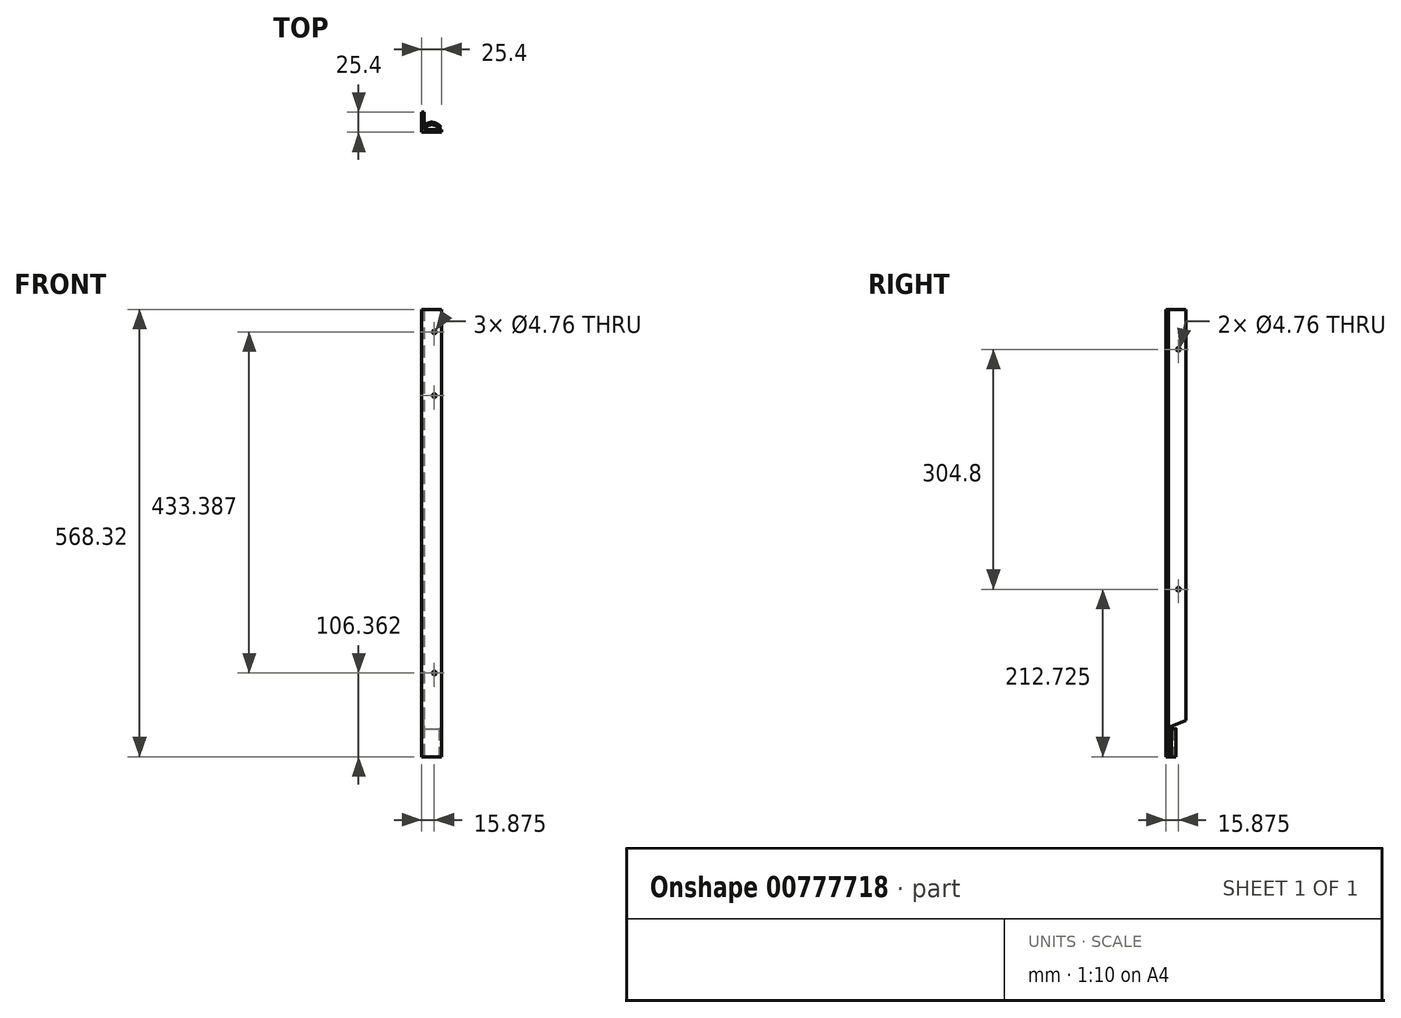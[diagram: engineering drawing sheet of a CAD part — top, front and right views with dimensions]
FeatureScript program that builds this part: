
annotation { "Feature Type Name" : "Feature", "Feature Type Description" : "" }
export const myFeature = defineFeature(function(context is Context, id is Id, definition is map)
    precondition{}
    {
        {
            var Q0;
            Q0=qCreatedBy(makeId("Top.planeOp"),FACE);
            var sketch = newSketch(context, id + "F0", { "sketchPlane" : qUnion([Q0])});
            skLineSegment(sketch, "E0.bottom", {"start": v(0, 0) * mm, "end": v(25.4, 0) * mm});
            skLineSegment(sketch, "E0.top", {"start": v(0, 25.4) * mm, "end": v(3.17, 25.4) * mm});
            skLineSegment(sketch, "E0.left", {"start": v(0, 0) * mm, "end": v(0, 25.4) * mm});
            skLineSegment(sketch, "E0.right", {"start": v(25.4, 0) * mm, "end": v(25.4, 3.18) * mm});
            skLineSegment(sketch, "E1.1", {"start": v(3.17, 3.18) * mm, "end": v(3.17, 25.4) * mm});
            skLineSegment(sketch, "E1.2", {"start": v(3.18, 3.18) * mm, "end": v(25.4, 3.18) * mm});
            skSolve(sketch);
        }
        {
            var Q0;
            Q0=qSketchRegion(id+"F0",true);
            extrude(context, id + "F1", {"entities" : qUnion([Q0]), "depth" : 568.32 * mm, "offsetDistance" : 25.4 * mm});
        }
        {
            var Q0;
            Q0=makeQuery(id+"F1.opExtrude","SWEPT_FACE",FACE,{"disambiguationData":[OSD([sQuery(id+"F0.wireOp",EDGE,"E0.left")])]});
            var sketch = newSketch(context, id + "F2", { "sketchPlane" : qUnion([Q0])});
            skCircle(sketch, "E2", {"center": v(-15.88, 517.53) * mm, "radius": 2.38 * mm});
            skCircle(sketch, "E3", {"center": v(-15.88, 212.73) * mm, "radius": 2.38 * mm});
            skSolve(sketch);
        }
        {
            var Q0;
            Q0=qSketchRegion(id+"F2",true);
            extrude(context, id + "F3", {"entities" : qUnion([Q0]), "operationType" : NewBodyOperationType.REMOVE, "oppositeDirection" : true, "depth" : 3.17 * mm, "offsetDistance" : 25.4 * mm});
        }
        {
            var Q0;
            Q0=makeQuery(id+"F1.opExtrude","SWEPT_FACE",FACE,{"disambiguationData":[OSD([sQuery(id+"F0.wireOp",EDGE,"E0.bottom")])]});
            var sketch = newSketch(context, id + "F4", { "sketchPlane" : qUnion([Q0])});
            skCircle(sketch, "E4", {"center": v(15.88, 458.79) * mm, "radius": 2.38 * mm});
            skCircle(sketch, "E5.0.1.0", {"center": v(15.88, 106.36) * mm, "radius": 2.38 * mm});
            skLineSegment(sketch, "E5.direction1", {"start": v(15.88, 458.79) * mm, "end": v(41.28, 458.79) * mm, "construction": true});
            skLineSegment(sketch, "E5.direction2", {"start": v(15.88, 458.79) * mm, "end": v(15.88, 106.36) * mm, "construction": true});
            skCircle(sketch, "E6", {"center": v(15.87, 539.75) * mm, "radius": 2.38 * mm});
            skSolve(sketch);
        }
        {
            var Q0;
            Q0=qSketchRegion(id+"F4",true);
            extrude(context, id + "F5", {"entities" : qUnion([Q0]), "operationType" : NewBodyOperationType.REMOVE, "oppositeDirection" : true, "depth" : 3.17 * mm, "offsetDistance" : 25.4 * mm});
        }
        {
            var Q0;
            Q0=makeQuery(id+"F1.opExtrude","SWEPT_FACE",FACE,{"disambiguationData":[OSD([sQuery(id+"F0.wireOp",EDGE,"E0.left")])]});
            var sketch = newSketch(context, id + "F6", { "sketchPlane" : qUnion([Q0])});
            skLineSegment(sketch, "E7", {"start": v(-4.76, 0) * mm, "end": v(-4.76, 38.1) * mm});
            skLineSegment(sketch, "E8", {"start": v(-4.76, 38.1) * mm, "end": v(-25.4, 46.44) * mm});
            skSolve(sketch);
        }
        {
            var Q0;
            Q0=qSketchRegion(id+"F6",true);
            var Q1;
            {var subQ0=sQuery(id+"F6.wireOp",EDGE,"E7");Q1=makeQuery(id+"F6.imprint","IMPRINT",FACE,{"disambiguationData":[TD([[makeQuery(id+"F6.imprint","IMPRINT",EDGE,{"derivedFrom":subQ0}),1.0]])]});}
            extrude(context, id + "F7", {"entities" : qUnion([Q0, Q1]), "operationType" : NewBodyOperationType.REMOVE, "oppositeDirection" : true, "depth" : 3.17 * mm, "offsetDistance" : 25.4 * mm});
        }
        {
            var Q0;
            Q0=makeQuery(id+"F1.opExtrude","CAP_FACE",FACE,{"disambiguationData":[OSD([sQuery(id+"F0.wireOp",EDGE,"E0.bottom"),sQuery(id+"F0.wireOp",EDGE,"E0.top"),sQuery(id+"F0.wireOp",EDGE,"E0.left"),sQuery(id+"F0.wireOp",EDGE,"E0.right"),sQuery(id+"F0.wireOp",EDGE,"E1.1"),sQuery(id+"F0.wireOp",EDGE,"E1.2")])],"isStart":true});
            var sketch = newSketch(context, id + "F8", { "sketchPlane" : qUnion([Q0])});
            skArc(sketch, "E9", {"start": v(12.36, -9.5) * mm, "mid": v(12.7, -9.53) * mm, "end": v(13.04, -9.5) * mm});
            skArc(sketch, "E10.0", {"start": v(12.01, -12.66) * mm, "mid": v(12.7, -12.7) * mm, "end": v(13.39, -12.66) * mm});
            skArc(sketch, "E11", {"start": v(0, -4.76) * mm, "mid": v(0.2, -5.89) * mm, "end": v(0.8, -6.87) * mm});
            skArc(sketch, "E12", {"start": v(0.8, -6.87) * mm, "mid": v(5.87, -10.81) * mm, "end": v(12.01, -12.66) * mm});
            skArc(sketch, "E13.0", {"start": v(3.17, -4.76) * mm, "mid": v(7.32, -7.99) * mm, "end": v(12.36, -9.5) * mm});
            skLineSegment(sketch, "E14", {"start": v(12.7, -6.35) * mm, "end": v(12.7, -13.47) * mm});
            skArc(sketch, "E15.MirrorCS", {"start": v(24.6, -6.87) * mm, "mid": v(19.53, -10.81) * mm, "end": v(13.39, -12.66) * mm});
            skArc(sketch, "E16.MirrorCS", {"start": v(22.23, -4.76) * mm, "mid": v(18.08, -7.99) * mm, "end": v(13.04, -9.5) * mm});
            skLineSegment(sketch, "E17", {"start": v(24.6, -6.87) * mm, "end": v(22.23, -4.76) * mm});
            skSolve(sketch);
        }
        {
            var Q0;
            Q0=qSketchRegion(id+"F8",true);
            var Q1;
            Q1=makeQuery(id+"F8.imprint","IMPRINT",FACE,{"disambiguationData":[TD([[makeQuery(id+"F8.imprint","IMPRINT",EDGE,{"derivedFrom":sQuery(id+"F8.wireOp",EDGE,"E11")}),1.0]])]});
            extrude(context, id + "F9", {"entities" : qUnion([Q0, Q1]), "operationType" : NewBodyOperationType.ADD, "oppositeDirection" : true, "depth" : 35.56 * mm, "offsetDistance" : 25.4 * mm});
        }
    });
